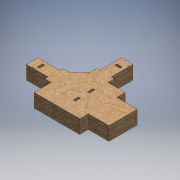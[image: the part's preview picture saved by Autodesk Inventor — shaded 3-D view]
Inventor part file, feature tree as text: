
AUTODESK INVENTOR PART (.ipt)
format: ipt  version: 2016 (Build 200138000, 138)  size: 192,512 bytes
history: native  units: mm
features: extrude x1
ambient origin geometry x8: Origin, YZ Plane, XZ Plane, XY Plane, X Axis, Y Axis, Z Axis, Center Point
bodies: Body1 (feature_tree)
feature tree (1):
  extrude  "Extrusion2"  Depth=1.5mm
